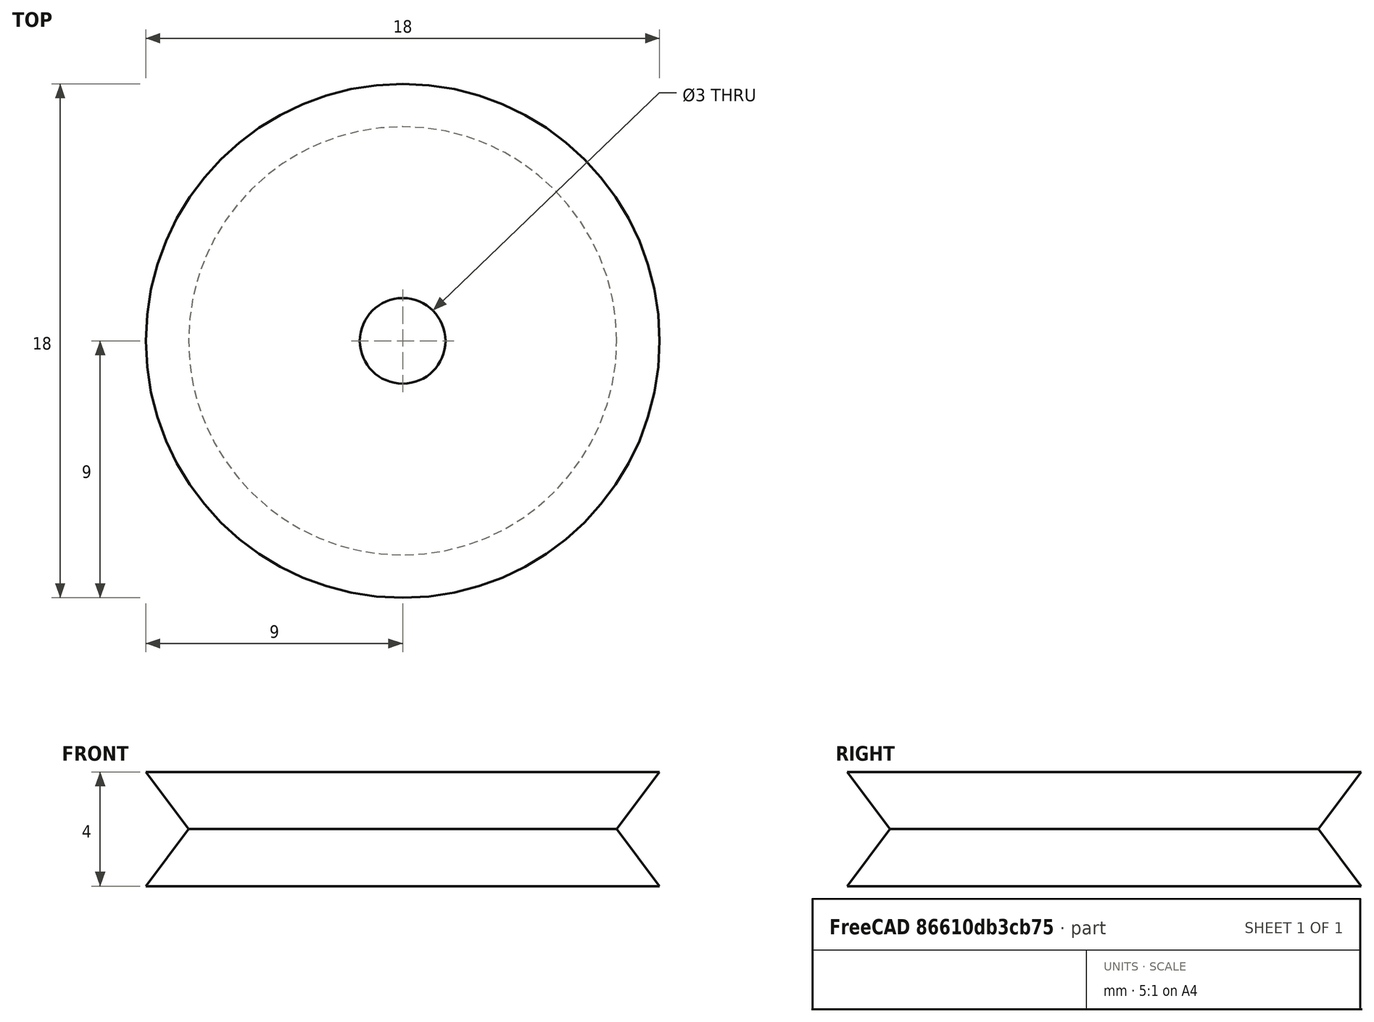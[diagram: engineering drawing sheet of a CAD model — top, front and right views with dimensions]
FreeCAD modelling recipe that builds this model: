
FCSTD DOCUMENT  (FreeCAD 0.18R16110 (Git))
Label: roller2
License: All rights reserved
LicenseURL: http://en.wikipedia.org/wiki/All_rights_reserved
objects: Sketcher::SketchObject×1, PartDesign::Revolution×1, PartDesign::Body×1
note: 4 computed .brp shape members not serialized (recipe doc carries the construction recipe); baked Part::Feature solids carry a one-line shape summary decoded from their .brp

FEATURE [Sketcher::SketchObject] Sketch
  MapMode = 5
  Placement = pos=(0,0,0) rot=(1,0,0;1.5708rad)
  Support = -> [XZ_Plane]
  sketch-geometry (5):
    g0: LineSegment StartX=1.5 StartY=0 StartZ=0 EndX=9 EndY=0 EndZ=0
    g1: LineSegment StartX=9 StartY=0 StartZ=0 EndX=7.5 EndY=2 EndZ=0
    g2: LineSegment StartX=7.5 StartY=2 StartZ=0 EndX=9 EndY=4 EndZ=0
    g3: LineSegment StartX=9 StartY=4 StartZ=0 EndX=1.5 EndY=4 EndZ=0
    g4: LineSegment StartX=1.5 StartY=4 StartZ=0 EndX=1.5 EndY=0 EndZ=0
  constraints (15):
    c: Coincident(g0,g1)
    c: Coincident(g1,g2)
    c: Coincident(g2,g3)
    c: Coincident(g3,g4)
    c: Coincident(g4,g0)
    c: Vertical(g4)
    c: Horizontal(g3)
    c: Horizontal(g0)
    c: PointOnObject(g0,g-1)
    c: Distance(g-1,g0) = 1.5
    c: DistanceY(g-1,g3) = 4
    c: DistanceX(g-1,g0) = 9
    c: DistanceX(g-1,g1) = 7.5
    c: Equal(g3,g0)
    c: DistanceY(g-1,g1) = 2
FEATURE [PartDesign::Revolution] Revolution
  Angle = 360
  Axis = (0,2e-16,1)
  Base = (0,0,0)
  Placement = pos=(0,0,0) rot=(1,0,0;1.5708rad)
  Profile = -> Sketch
  ReferenceAxis = -> Sketch [V_Axis]
  Reversed = true
FEATURE [PartDesign::Body] Body
  Group = -> [Sketch,Revolution]
  Origin = -> Origin
  Tip = -> Revolution
